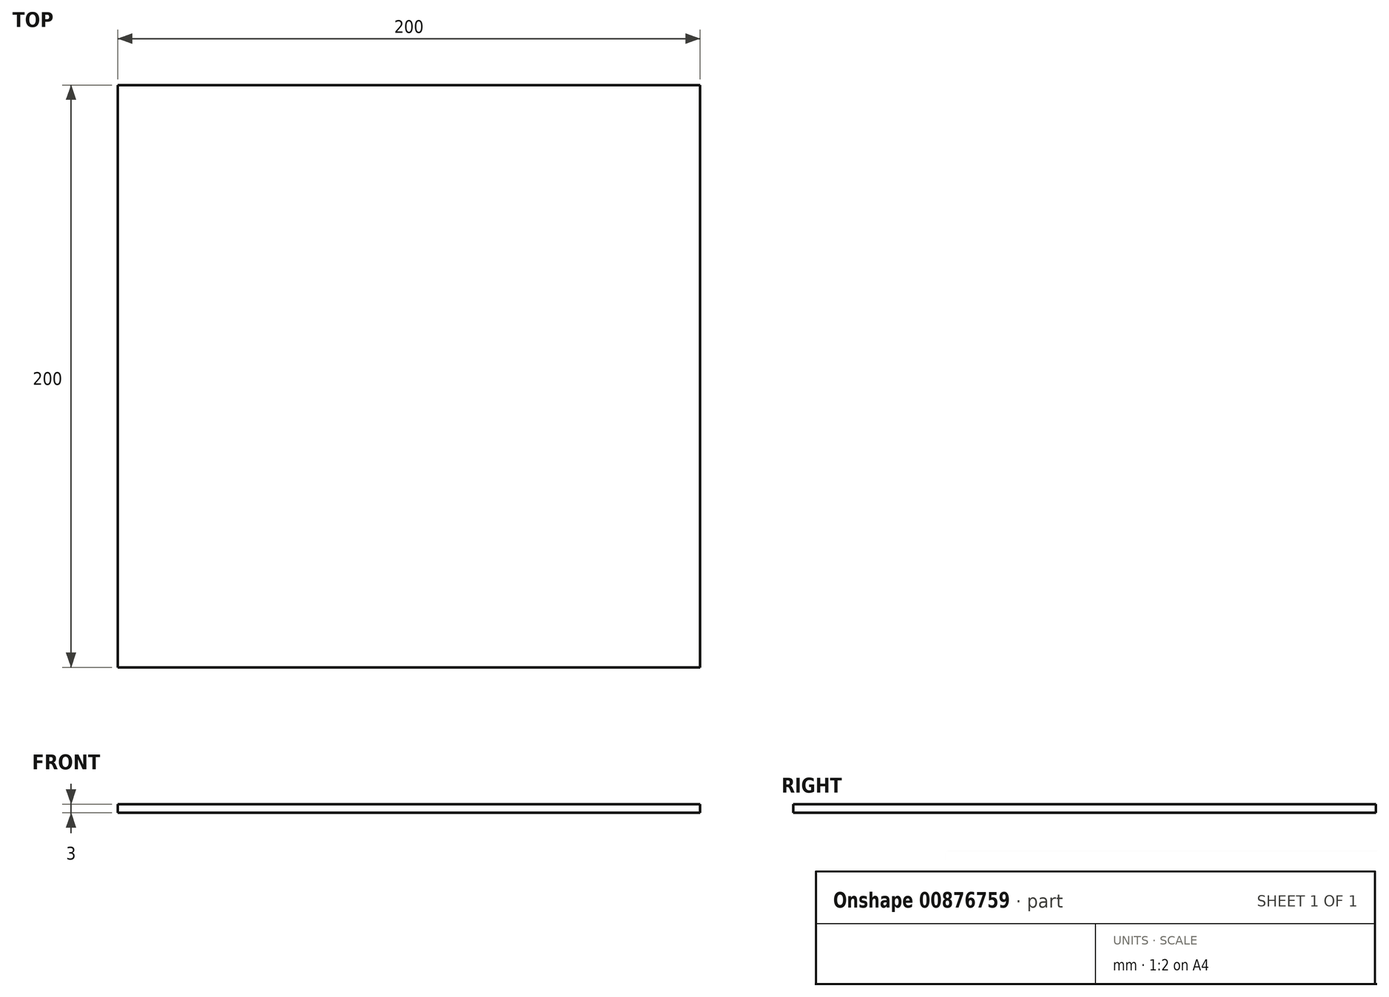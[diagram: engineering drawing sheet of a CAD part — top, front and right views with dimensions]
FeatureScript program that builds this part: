
annotation { "Feature Type Name" : "Feature", "Feature Type Description" : "" }
export const myFeature = defineFeature(function(context is Context, id is Id, definition is map)
    precondition{}
    {
        {
            var Q0;
            Q0=qCreatedBy(makeId("Top.planeOp"),FACE);
            var sketch = newSketch(context, id + "F0", { "sketchPlane" : qUnion([Q0])});
            skLineSegment(sketch, "E0.bottom", {"start": v(-100.15, 121.66) * mm, "end": v(99.85, 121.66) * mm});
            skLineSegment(sketch, "E0.top", {"start": v(-100.15, -78.34) * mm, "end": v(99.85, -78.34) * mm});
            skLineSegment(sketch, "E0.left", {"start": v(-100.15, 121.66) * mm, "end": v(-100.15, -78.34) * mm});
            skLineSegment(sketch, "E0.right", {"start": v(99.85, 121.66) * mm, "end": v(99.85, -78.34) * mm});
            skSolve(sketch);
        }
        {
            var Q0;
            Q0 = qSketchRegion(id + "F0", true);
            extrude(context, id + "F1", {"entities" : qUnion([Q0]), "depth" : 3 * mm, "offsetDistance" : 25.4 * mm});
        }
    });
